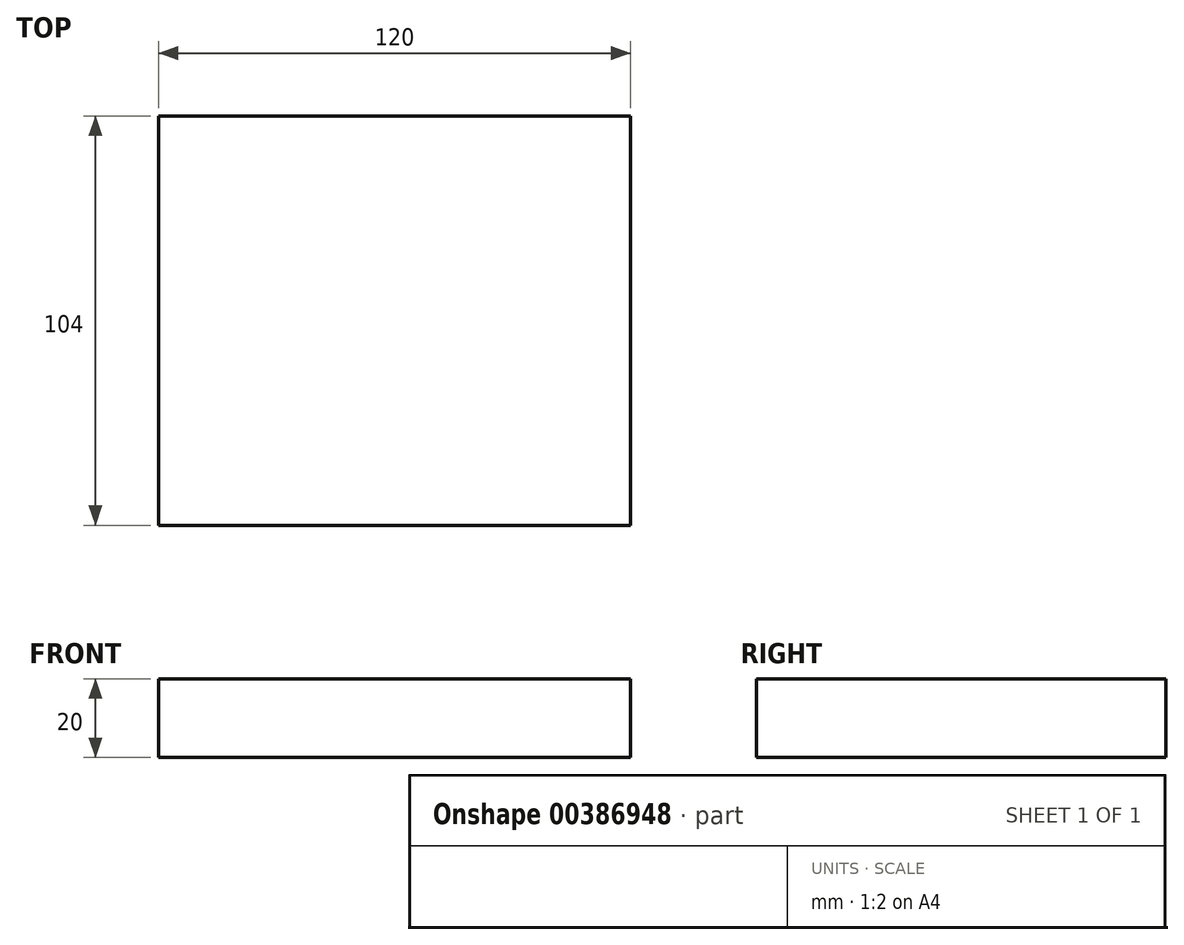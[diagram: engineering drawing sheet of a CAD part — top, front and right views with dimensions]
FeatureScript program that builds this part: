
annotation { "Feature Type Name" : "Feature", "Feature Type Description" : "" }
export const myFeature = defineFeature(function(context is Context, id is Id, definition is map)
    precondition{}
    {
        {
            var Q0;
            Q0=qCreatedBy(makeId("Top.planeOp"),FACE);
            var sketch = newSketch(context, id + "F0", { "sketchPlane" : qUnion([Q0])});
            skLineSegment(sketch, "E0.bottom", {"start": v(-60, 52) * mm, "end": v(60, 52) * mm});
            skLineSegment(sketch, "E0.top", {"start": v(-60, -52) * mm, "end": v(60, -52) * mm});
            skLineSegment(sketch, "E0.left", {"start": v(-60, 52) * mm, "end": v(-60, -52) * mm});
            skLineSegment(sketch, "E0.right", {"start": v(60, 52) * mm, "end": v(60, -52) * mm});
            skPoint(sketch, "E0.middle", {"position": v(0, 0) * mm});
            skSolve(sketch);
        }
        {
            var Q0;
            Q0 = qSketchRegion(id + "F0", true);
            extrude(context, id + "F1", {"entities" : qUnion([Q0]), "depth" : 20 * mm});
        }
    });
